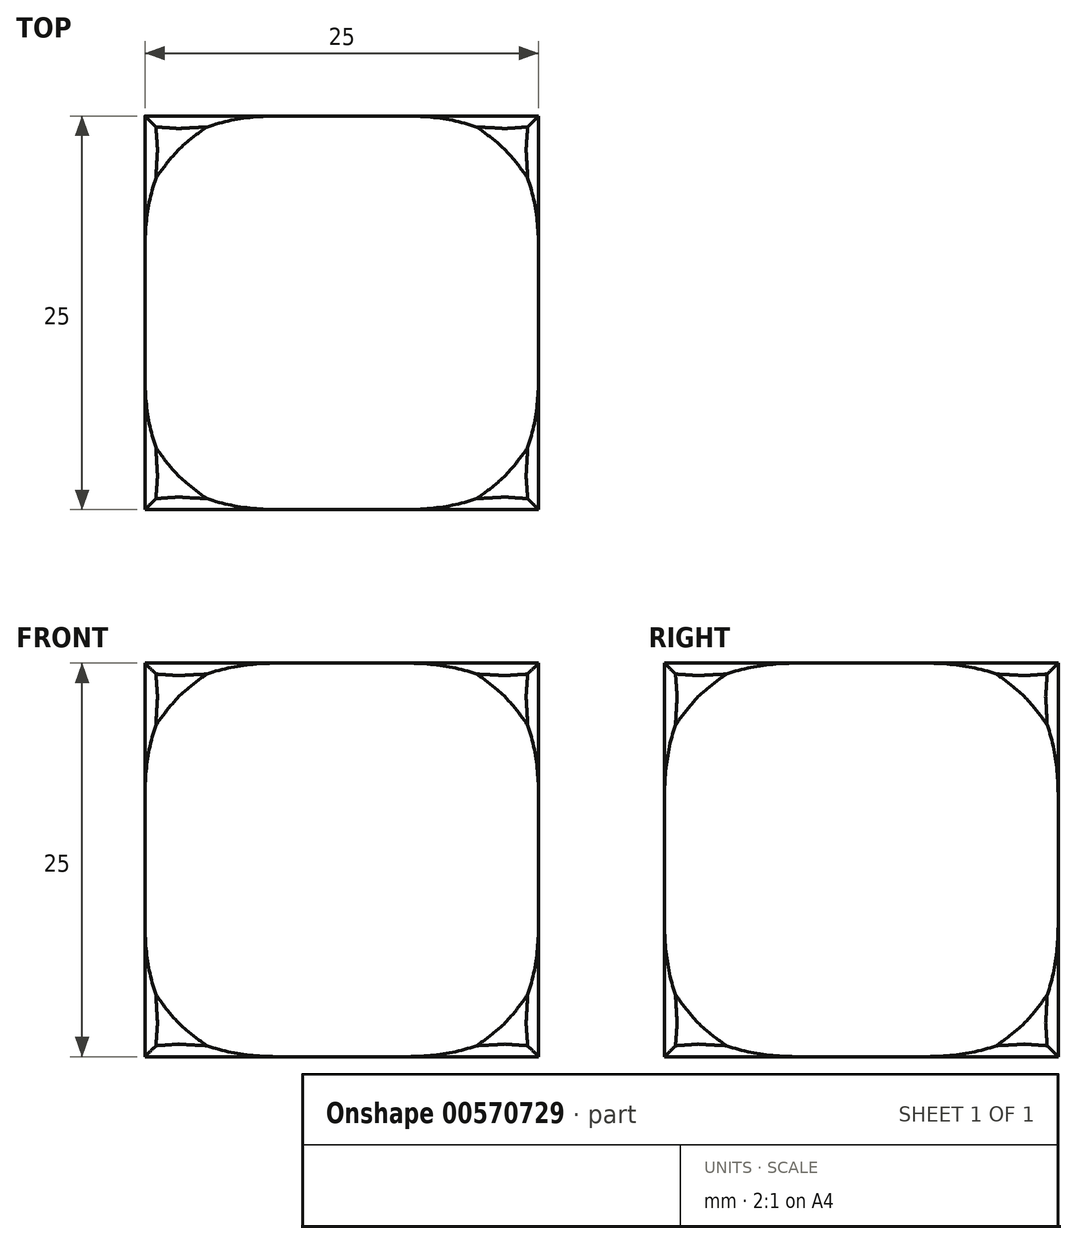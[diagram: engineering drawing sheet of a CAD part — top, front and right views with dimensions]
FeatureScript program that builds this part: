
annotation { "Feature Type Name" : "Feature", "Feature Type Description" : "" }
export const myFeature = defineFeature(function(context is Context, id is Id, definition is map)
    precondition{}
    {
        {
            var Q0;
            Q0=qCreatedBy(makeId("Top.planeOp"),FACE);
            var sketch = newSketch(context, id + "F0", { "sketchPlane" : qUnion([Q0])});
            skLineSegment(sketch, "E0.bottom", {"start": v(-8.3, -12.5) * mm, "end": v(8.3, -12.5) * mm});
            skLineSegment(sketch, "E0.top", {"start": v(-8.3, 12.5) * mm, "end": v(8.3, 12.5) * mm});
            skLineSegment(sketch, "E0.left", {"start": v(-12.5, -8.3) * mm, "end": v(-12.5, 8.3) * mm});
            skLineSegment(sketch, "E0.right", {"start": v(12.5, -8.3) * mm, "end": v(12.5, 8.3) * mm});
            skPoint(sketch, "E0.middle", {"position": v(0, 0) * mm});
            skArc(sketch, "E1", {"start": v(-8.3, 12.5) * mm, "mid": v(-10.6, 10.6) * mm, "end": v(-12.5, 8.3) * mm});
            skPoint(sketch, "E2.orphan", {"position": v(-12.5, 12.5) * mm});
            skPoint(sketch, "E3.orphan", {"position": v(12.5, 12.5) * mm});
            skArc(sketch, "E4.trimOffspring", {"start": v(12.5, 8.3) * mm, "mid": v(10.6, 10.6) * mm, "end": v(8.3, 12.5) * mm});
            skPoint(sketch, "E5.orphan", {"position": v(12.5, -12.5) * mm});
            skArc(sketch, "E6.trimOffspring", {"start": v(8.3, -12.5) * mm, "mid": v(10.6, -10.6) * mm, "end": v(12.5, -8.3) * mm});
            skPoint(sketch, "E7.orphan", {"position": v(-12.5, -12.5) * mm});
            skArc(sketch, "E8.trimOffspring", {"start": v(-12.5, -8.3) * mm, "mid": v(-10.6, -10.6) * mm, "end": v(-8.3, -12.5) * mm});
            skSolve(sketch);
        }
        {
            var Q0;
            Q0=makeQuery(id+"F0.imprint","IMPRINT",FACE,{"disambiguationData":[TD([[makeQuery(id+"F0.imprint","IMPRINT",EDGE,{"derivedFrom":sQuery(id+"F0.wireOp",EDGE,"E0.bottom")}),1.0]])]});
            extrude(context, id + "F1", {"entities" : qUnion([Q0]), "depth" : 25 * mm, "offsetDistance" : 25 * mm});
        }
        {
            var Q0;
            Q0=makeQuery(id+"F1.opExtrude","SWEPT_FACE",FACE,{"disambiguationData":[OSD([sQuery(id+"F0.wireOp",EDGE,"E0.left")])]});
            var sketch = newSketch(context, id + "F2", { "sketchPlane" : qUnion([Q0])});
            skLineSegment(sketch, "E9.bottom", {"start": v(8.3, 0) * mm, "end": v(-8.3, 0) * mm});
            skLineSegment(sketch, "E9.top", {"start": v(8.3, 25) * mm, "end": v(-8.3, 25) * mm});
            skLineSegment(sketch, "E9.left", {"start": v(12.5, 4.2) * mm, "end": v(12.5, 20.8) * mm});
            skLineSegment(sketch, "E9.right", {"start": v(-12.5, 4.2) * mm, "end": v(-12.5, 25) * mm});
            skPoint(sketch, "E9.middle", {"position": v(0, 12.5) * mm});
            skPoint(sketch, "E9.middle.positionSnap0", {"position": v(-8.3, 12.5) * mm});
            skPoint(sketch, "E9.centerSnap0", {"position": v(-8.3, 12.5) * mm});
            skArc(sketch, "E10", {"start": v(-12.5, 4.2) * mm, "mid": v(-10.6, 1.9) * mm, "end": v(-8.3, 0) * mm});
            skPoint(sketch, "E11.orphan", {"position": v(-12.5, 0) * mm});
            skArc(sketch, "E12.trimOffspring", {"start": v(8.3, 0) * mm, "mid": v(10.6, 1.9) * mm, "end": v(12.5, 4.2) * mm});
            skArc(sketch, "E13.trimOffspring", {"start": v(12.5, 20.8) * mm, "mid": v(10.6, 23.1) * mm, "end": v(8.3, 25) * mm});
            skArc(sketch, "E14.trimOffspring", {"start": v(-8.3, 25) * mm, "mid": v(-10.6, 23.1) * mm, "end": v(-12.5, 20.8) * mm});
            skPoint(sketch, "E15.orphan", {"position": v(12.5, 25) * mm});
            skPoint(sketch, "E16.orphan", {"position": v(12.5, 0) * mm});
            skSolve(sketch);
        }
        {
            var Q0;
            Q0=qSketchRegion(id+"F2",true);
            extrude(context, id + "F3", {"entities" : qUnion([Q0]), "operationType" : NewBodyOperationType.ADD, "oppositeDirection" : true, "depth" : 25 * mm, "offsetDistance" : 25 * mm});
        }
        {
            var Q0;
            Q0=makeQuery(id+"F3.boolean.opBoolean","MERGE",FACE,{"derivedFrom":[makeQuery(id+"F1.opExtrude","SWEPT_FACE",FACE,{"disambiguationData":[OSD([sQuery(id+"F0.wireOp",EDGE,"E0.top")])]}),makeQuery(id+"F3.opExtrude","SWEPT_FACE",FACE,{"disambiguationData":[OSD([sQuery(id+"F2.wireOp",EDGE,"E9.right")])]})]});
            var sketch = newSketch(context, id + "F4", { "sketchPlane" : qUnion([Q0])});
            skLineSegment(sketch, "E17.bottom", {"start": v(-8.3, 0) * mm, "end": v(8.3, 0) * mm});
            skLineSegment(sketch, "E17.top", {"start": v(-8.3, 25) * mm, "end": v(8.3, 25) * mm});
            skLineSegment(sketch, "E17.left", {"start": v(-12.5, 4.2) * mm, "end": v(-12.5, 20.8) * mm});
            skLineSegment(sketch, "E17.right", {"start": v(12.5, 4.2) * mm, "end": v(12.5, 20.8) * mm});
            skPoint(sketch, "E17.middle", {"position": v(0, 12.5) * mm});
            skPoint(sketch, "E17.middle.positionSnap0", {"position": v(-12.5, 12.5) * mm});
            skPoint(sketch, "E17.middle.positionSnap1", {"position": v(0, 25) * mm});
            skPoint(sketch, "E17.centerSnap0", {"position": v(-12.5, 12.5) * mm});
            skPoint(sketch, "E17.centerSnap1", {"position": v(0, 25) * mm});
            skArc(sketch, "E18", {"start": v(-8.3, 25) * mm, "mid": v(-10.6, 23.1) * mm, "end": v(-12.5, 20.8) * mm});
            skPoint(sketch, "E19.orphan", {"position": v(-12.5, 25) * mm});
            skArc(sketch, "E20.trimOffspring", {"start": v(-12.5, 4.2) * mm, "mid": v(-10.6, 1.9) * mm, "end": v(-8.3, 0) * mm});
            skPoint(sketch, "E21.orphan", {"position": v(-12.5, 0) * mm});
            skArc(sketch, "E22.trimOffspring", {"start": v(8.3, 0) * mm, "mid": v(10.6, 1.9) * mm, "end": v(12.5, 4.2) * mm});
            skPoint(sketch, "E23.orphan", {"position": v(12.5, 0) * mm});
            skArc(sketch, "E24.trimOffspring", {"start": v(12.5, 20.8) * mm, "mid": v(10.6, 23.1) * mm, "end": v(8.3, 25) * mm});
            skPoint(sketch, "E25.orphan", {"position": v(12.5, 25) * mm});
            skSolve(sketch);
        }
        {
            var Q0;
            Q0=qSketchRegion(id+"F4",true);
            extrude(context, id + "F5", {"entities" : qUnion([Q0]), "operationType" : NewBodyOperationType.ADD, "oppositeDirection" : true, "depth" : 25 * mm, "offsetDistance" : 25 * mm});
        }
        {
            var Q0;
            Q0=makeQuery(id+"F5.opExtrude","CAP_EDGE",EDGE,{"disambiguationData":[OSD([sQuery(id+"F4.wireOp",EDGE,"E18")])],"isStart":false});
            var Q1;
            Q1=makeQuery(id+"F1.opExtrude","CAP_EDGE",EDGE,{"disambiguationData":[OSD([sQuery(id+"F0.wireOp",EDGE,"E6.trimOffspring")])],"isStart":false});
            var Q2;
            Q2=makeQuery(id+"F3.opExtrude","CAP_EDGE",EDGE,{"disambiguationData":[OSD([sQuery(id+"F2.wireOp",EDGE,"E13.trimOffspring")])],"isStart":false});
            var Q3;
            Q3=makeQuery(id+"F5.opExtrude","CAP_EDGE",EDGE,{"disambiguationData":[OSD([sQuery(id+"F4.wireOp",EDGE,"E24.trimOffspring")])],"isStart":false});
            var Q4;
            Q4=makeQuery(id+"F1.opExtrude","CAP_EDGE",EDGE,{"disambiguationData":[OSD([sQuery(id+"F0.wireOp",EDGE,"E8.trimOffspring")])],"isStart":false});
            var Q5;
            Q5=makeQuery(id+"F3.opExtrude","CAP_EDGE",EDGE,{"disambiguationData":[OSD([sQuery(id+"F2.wireOp",EDGE,"E13.trimOffspring")])],"isStart":true});
            var Q6;
            Q6=makeQuery(id+"F5.opExtrude","CAP_EDGE",EDGE,{"disambiguationData":[OSD([sQuery(id+"F4.wireOp",EDGE,"E22.trimOffspring")])],"isStart":false});
            var Q7;
            Q7=makeQuery(id+"F3.opExtrude","CAP_EDGE",EDGE,{"disambiguationData":[OSD([sQuery(id+"F2.wireOp",EDGE,"E12.trimOffspring")])],"isStart":true});
            var Q8;
            Q8=makeQuery(id+"F1.opExtrude","CAP_EDGE",EDGE,{"disambiguationData":[OSD([sQuery(id+"F0.wireOp",EDGE,"E8.trimOffspring")])],"isStart":true});
            var Q9;
            Q9=makeQuery(id+"F5.opExtrude","CAP_EDGE",EDGE,{"disambiguationData":[OSD([sQuery(id+"F4.wireOp",EDGE,"E20.trimOffspring")])],"isStart":false});
            var Q10;
            Q10=makeQuery(id+"F1.opExtrude","CAP_EDGE",EDGE,{"disambiguationData":[OSD([sQuery(id+"F0.wireOp",EDGE,"E6.trimOffspring")])],"isStart":true});
            var Q11;
            Q11=makeQuery(id+"F3.opExtrude","CAP_EDGE",EDGE,{"disambiguationData":[OSD([sQuery(id+"F2.wireOp",EDGE,"E12.trimOffspring")])],"isStart":false});
            var Q12;
            Q12=makeQuery(id+"F3.opExtrude","CAP_EDGE",EDGE,{"disambiguationData":[OSD([sQuery(id+"F2.wireOp",EDGE,"E10")])],"isStart":false});
            var Q13;
            Q13=makeQuery(id+"F5.opExtrude","CAP_EDGE",EDGE,{"disambiguationData":[OSD([sQuery(id+"F4.wireOp",EDGE,"E20.trimOffspring")])],"isStart":true});
            var Q14;
            Q14=makeQuery(id+"F1.opExtrude","CAP_EDGE",EDGE,{"disambiguationData":[OSD([sQuery(id+"F0.wireOp",EDGE,"E4.trimOffspring")])],"isStart":true});
            var Q15;
            Q15=makeQuery(id+"F3.opExtrude","CAP_EDGE",EDGE,{"disambiguationData":[OSD([sQuery(id+"F2.wireOp",EDGE,"E14.trimOffspring")])],"isStart":false});
            var Q16;
            Q16=makeQuery(id+"F5.opExtrude","CAP_EDGE",EDGE,{"disambiguationData":[OSD([sQuery(id+"F4.wireOp",EDGE,"E18")])],"isStart":true});
            var Q17;
            Q17=makeQuery(id+"F1.opExtrude","CAP_EDGE",EDGE,{"disambiguationData":[OSD([sQuery(id+"F0.wireOp",EDGE,"E4.trimOffspring")])],"isStart":false});
            var Q18;
            Q18=makeQuery(id+"F1.opExtrude","CAP_EDGE",EDGE,{"disambiguationData":[OSD([sQuery(id+"F0.wireOp",EDGE,"E1")])],"isStart":false});
            var Q19;
            Q19=makeQuery(id+"F5.opExtrude","CAP_EDGE",EDGE,{"disambiguationData":[OSD([sQuery(id+"F4.wireOp",EDGE,"E24.trimOffspring")])],"isStart":true});
            var Q20;
            Q20=makeQuery(id+"F3.opExtrude","CAP_EDGE",EDGE,{"disambiguationData":[OSD([sQuery(id+"F2.wireOp",EDGE,"E14.trimOffspring")])],"isStart":true});
            var Q21;
            Q21=makeQuery(id+"F3.opExtrude","CAP_EDGE",EDGE,{"disambiguationData":[OSD([sQuery(id+"F2.wireOp",EDGE,"E10")])],"isStart":true});
            var Q22;
            Q22=makeQuery(id+"F5.opExtrude","CAP_EDGE",EDGE,{"disambiguationData":[OSD([sQuery(id+"F4.wireOp",EDGE,"E22.trimOffspring")])],"isStart":true});
            var Q23;
            Q23=makeQuery(id+"F1.opExtrude","CAP_EDGE",EDGE,{"disambiguationData":[OSD([sQuery(id+"F0.wireOp",EDGE,"E1")])],"isStart":true});
            fillet(context, id + "F6", {"entities" : qUnion([Q0, Q1, Q2, Q3, Q4, Q5, Q6, Q7, Q8, Q9, Q10, Q11, Q12, Q13, Q14, Q15, Q16, Q17, Q18, Q19, Q20, Q21, Q22, Q23]), "radius" : 1.88 * mm, "tangentPropagation" : true, "allowEdgeOverflow" : false});
        }
        {
            var Q0;
            Q0=makeQuery(id+"F6.opFillet","BLEND_EDGE",EDGE,{"disambiguationData":[OD(1.0)],"blendedFrom":[makeQuery(id+"F1.opExtrude","CAP_EDGE",EDGE,{"disambiguationData":[OSD([sQuery(id+"F0.wireOp",EDGE,"E6.trimOffspring")])],"isStart":false}),makeQuery(id+"F5.opExtrude","CAP_EDGE",EDGE,{"disambiguationData":[OSD([sQuery(id+"F4.wireOp",EDGE,"E18")])],"isStart":false})],"blendedInto":[]});
            var Q1;
            Q1=makeQuery(id+"F6.opFillet","BLEND_EDGE",EDGE,{"disambiguationData":[OD(1.0)],"blendedFrom":[makeQuery(id+"F1.opExtrude","CAP_EDGE",EDGE,{"disambiguationData":[OSD([sQuery(id+"F0.wireOp",EDGE,"E6.trimOffspring")])],"isStart":false}),makeQuery(id+"F3.opExtrude","CAP_EDGE",EDGE,{"disambiguationData":[OSD([sQuery(id+"F2.wireOp",EDGE,"E13.trimOffspring")])],"isStart":false})],"blendedInto":[]});
            var Q2;
            Q2=makeQuery(id+"F6.opFillet","BLEND_EDGE",EDGE,{"disambiguationData":[OD(1.0)],"blendedFrom":[makeQuery(id+"F3.opExtrude","CAP_EDGE",EDGE,{"disambiguationData":[OSD([sQuery(id+"F2.wireOp",EDGE,"E13.trimOffspring")])],"isStart":false}),makeQuery(id+"F5.opExtrude","CAP_EDGE",EDGE,{"disambiguationData":[OSD([sQuery(id+"F4.wireOp",EDGE,"E18")])],"isStart":false})],"blendedInto":[]});
            var Q3;
            Q3=makeQuery(id+"F6.opFillet","BLEND_EDGE",EDGE,{"disambiguationData":[OD(1.0)],"blendedFrom":[makeQuery(id+"F1.opExtrude","CAP_EDGE",EDGE,{"disambiguationData":[OSD([sQuery(id+"F0.wireOp",EDGE,"E8.trimOffspring")])],"isStart":false}),makeQuery(id+"F5.opExtrude","CAP_EDGE",EDGE,{"disambiguationData":[OSD([sQuery(id+"F4.wireOp",EDGE,"E24.trimOffspring")])],"isStart":false})],"blendedInto":[]});
            var Q4;
            Q4=makeQuery(id+"F6.opFillet","BLEND_EDGE",EDGE,{"disambiguationData":[OD(1.0)],"blendedFrom":[makeQuery(id+"F1.opExtrude","CAP_EDGE",EDGE,{"disambiguationData":[OSD([sQuery(id+"F0.wireOp",EDGE,"E8.trimOffspring")])],"isStart":false}),makeQuery(id+"F3.opExtrude","CAP_EDGE",EDGE,{"disambiguationData":[OSD([sQuery(id+"F2.wireOp",EDGE,"E13.trimOffspring")])],"isStart":true})],"blendedInto":[]});
            var Q5;
            Q5=makeQuery(id+"F6.opFillet","BLEND_EDGE",EDGE,{"disambiguationData":[OD(1.0)],"blendedFrom":[makeQuery(id+"F3.opExtrude","CAP_EDGE",EDGE,{"disambiguationData":[OSD([sQuery(id+"F2.wireOp",EDGE,"E13.trimOffspring")])],"isStart":true}),makeQuery(id+"F5.opExtrude","CAP_EDGE",EDGE,{"disambiguationData":[OSD([sQuery(id+"F4.wireOp",EDGE,"E24.trimOffspring")])],"isStart":false})],"blendedInto":[]});
            var Q6;
            Q6=makeQuery(id+"F6.opFillet","BLEND_EDGE",EDGE,{"disambiguationData":[OD(1.0)],"blendedFrom":[makeQuery(id+"F3.opExtrude","CAP_EDGE",EDGE,{"disambiguationData":[OSD([sQuery(id+"F2.wireOp",EDGE,"E12.trimOffspring")])],"isStart":true}),makeQuery(id+"F5.opExtrude","CAP_EDGE",EDGE,{"disambiguationData":[OSD([sQuery(id+"F4.wireOp",EDGE,"E22.trimOffspring")])],"isStart":false})],"blendedInto":[]});
            var Q7;
            Q7=makeQuery(id+"F6.opFillet","BLEND_EDGE",EDGE,{"disambiguationData":[OD(1.0)],"blendedFrom":[makeQuery(id+"F1.opExtrude","CAP_EDGE",EDGE,{"disambiguationData":[OSD([sQuery(id+"F0.wireOp",EDGE,"E8.trimOffspring")])],"isStart":true}),makeQuery(id+"F5.opExtrude","CAP_EDGE",EDGE,{"disambiguationData":[OSD([sQuery(id+"F4.wireOp",EDGE,"E22.trimOffspring")])],"isStart":false})],"blendedInto":[]});
            var Q8;
            Q8=makeQuery(id+"F6.opFillet","BLEND_EDGE",EDGE,{"disambiguationData":[OD(1.0)],"blendedFrom":[makeQuery(id+"F1.opExtrude","CAP_EDGE",EDGE,{"disambiguationData":[OSD([sQuery(id+"F0.wireOp",EDGE,"E8.trimOffspring")])],"isStart":true}),makeQuery(id+"F3.opExtrude","CAP_EDGE",EDGE,{"disambiguationData":[OSD([sQuery(id+"F2.wireOp",EDGE,"E12.trimOffspring")])],"isStart":true})],"blendedInto":[]});
            var Q9;
            Q9=makeQuery(id+"F6.opFillet","BLEND_EDGE",EDGE,{"disambiguationData":[OD(1.0)],"blendedFrom":[makeQuery(id+"F1.opExtrude","CAP_EDGE",EDGE,{"disambiguationData":[OSD([sQuery(id+"F0.wireOp",EDGE,"E6.trimOffspring")])],"isStart":true}),makeQuery(id+"F5.opExtrude","CAP_EDGE",EDGE,{"disambiguationData":[OSD([sQuery(id+"F4.wireOp",EDGE,"E20.trimOffspring")])],"isStart":false})],"blendedInto":[]});
            var Q10;
            Q10=makeQuery(id+"F6.opFillet","BLEND_EDGE",EDGE,{"disambiguationData":[OD(1.0)],"blendedFrom":[makeQuery(id+"F3.opExtrude","CAP_EDGE",EDGE,{"disambiguationData":[OSD([sQuery(id+"F2.wireOp",EDGE,"E12.trimOffspring")])],"isStart":false}),makeQuery(id+"F5.opExtrude","CAP_EDGE",EDGE,{"disambiguationData":[OSD([sQuery(id+"F4.wireOp",EDGE,"E20.trimOffspring")])],"isStart":false})],"blendedInto":[]});
            var Q11;
            Q11=makeQuery(id+"F6.opFillet","BLEND_EDGE",EDGE,{"disambiguationData":[OD(1.0)],"blendedFrom":[makeQuery(id+"F1.opExtrude","CAP_EDGE",EDGE,{"disambiguationData":[OSD([sQuery(id+"F0.wireOp",EDGE,"E6.trimOffspring")])],"isStart":true}),makeQuery(id+"F3.opExtrude","CAP_EDGE",EDGE,{"disambiguationData":[OSD([sQuery(id+"F2.wireOp",EDGE,"E12.trimOffspring")])],"isStart":false})],"blendedInto":[]});
            var Q12;
            Q12=makeQuery(id+"F6.opFillet","BLEND_EDGE",EDGE,{"disambiguationData":[OD(1.0)],"blendedFrom":[makeQuery(id+"F1.opExtrude","CAP_EDGE",EDGE,{"disambiguationData":[OSD([sQuery(id+"F0.wireOp",EDGE,"E4.trimOffspring")])],"isStart":true}),makeQuery(id+"F5.opExtrude","CAP_EDGE",EDGE,{"disambiguationData":[OSD([sQuery(id+"F4.wireOp",EDGE,"E20.trimOffspring")])],"isStart":true})],"blendedInto":[]});
            var Q13;
            Q13=makeQuery(id+"F6.opFillet","BLEND_EDGE",EDGE,{"disambiguationData":[OD(1.0)],"blendedFrom":[makeQuery(id+"F1.opExtrude","CAP_EDGE",EDGE,{"disambiguationData":[OSD([sQuery(id+"F0.wireOp",EDGE,"E4.trimOffspring")])],"isStart":true}),makeQuery(id+"F3.opExtrude","CAP_EDGE",EDGE,{"disambiguationData":[OSD([sQuery(id+"F2.wireOp",EDGE,"E10")])],"isStart":false})],"blendedInto":[]});
            var Q14;
            Q14=makeQuery(id+"F6.opFillet","BLEND_EDGE",EDGE,{"disambiguationData":[OD(1.0)],"blendedFrom":[makeQuery(id+"F3.opExtrude","CAP_EDGE",EDGE,{"disambiguationData":[OSD([sQuery(id+"F2.wireOp",EDGE,"E10")])],"isStart":false}),makeQuery(id+"F5.opExtrude","CAP_EDGE",EDGE,{"disambiguationData":[OSD([sQuery(id+"F4.wireOp",EDGE,"E20.trimOffspring")])],"isStart":true})],"blendedInto":[]});
            var Q15;
            Q15=makeQuery(id+"F6.opFillet","BLEND_EDGE",EDGE,{"disambiguationData":[OD(1.0)],"blendedFrom":[makeQuery(id+"F1.opExtrude","CAP_EDGE",EDGE,{"disambiguationData":[OSD([sQuery(id+"F0.wireOp",EDGE,"E1")])],"isStart":true}),makeQuery(id+"F5.opExtrude","CAP_EDGE",EDGE,{"disambiguationData":[OSD([sQuery(id+"F4.wireOp",EDGE,"E22.trimOffspring")])],"isStart":true})],"blendedInto":[]});
            var Q16;
            Q16=makeQuery(id+"F6.opFillet","BLEND_EDGE",EDGE,{"disambiguationData":[OD(1.0)],"blendedFrom":[makeQuery(id+"F1.opExtrude","CAP_EDGE",EDGE,{"disambiguationData":[OSD([sQuery(id+"F0.wireOp",EDGE,"E1")])],"isStart":true}),makeQuery(id+"F3.opExtrude","CAP_EDGE",EDGE,{"disambiguationData":[OSD([sQuery(id+"F2.wireOp",EDGE,"E10")])],"isStart":true})],"blendedInto":[]});
            var Q17;
            Q17=makeQuery(id+"F6.opFillet","BLEND_EDGE",EDGE,{"disambiguationData":[OD(1.0)],"blendedFrom":[makeQuery(id+"F3.opExtrude","CAP_EDGE",EDGE,{"disambiguationData":[OSD([sQuery(id+"F2.wireOp",EDGE,"E10")])],"isStart":true}),makeQuery(id+"F5.opExtrude","CAP_EDGE",EDGE,{"disambiguationData":[OSD([sQuery(id+"F4.wireOp",EDGE,"E22.trimOffspring")])],"isStart":true})],"blendedInto":[]});
            var Q18;
            Q18=makeQuery(id+"F6.opFillet","BLEND_EDGE",EDGE,{"disambiguationData":[OD(1.0)],"blendedFrom":[makeQuery(id+"F1.opExtrude","CAP_EDGE",EDGE,{"disambiguationData":[OSD([sQuery(id+"F0.wireOp",EDGE,"E4.trimOffspring")])],"isStart":false}),makeQuery(id+"F5.opExtrude","CAP_EDGE",EDGE,{"disambiguationData":[OSD([sQuery(id+"F4.wireOp",EDGE,"E18")])],"isStart":true})],"blendedInto":[]});
            var Q19;
            Q19=makeQuery(id+"F6.opFillet","BLEND_EDGE",EDGE,{"disambiguationData":[OD(1.0)],"blendedFrom":[makeQuery(id+"F3.opExtrude","CAP_EDGE",EDGE,{"disambiguationData":[OSD([sQuery(id+"F2.wireOp",EDGE,"E14.trimOffspring")])],"isStart":false}),makeQuery(id+"F5.opExtrude","CAP_EDGE",EDGE,{"disambiguationData":[OSD([sQuery(id+"F4.wireOp",EDGE,"E18")])],"isStart":true})],"blendedInto":[]});
            var Q20;
            Q20=makeQuery(id+"F6.opFillet","BLEND_EDGE",EDGE,{"disambiguationData":[OD(1.0)],"blendedFrom":[makeQuery(id+"F1.opExtrude","CAP_EDGE",EDGE,{"disambiguationData":[OSD([sQuery(id+"F0.wireOp",EDGE,"E4.trimOffspring")])],"isStart":false}),makeQuery(id+"F3.opExtrude","CAP_EDGE",EDGE,{"disambiguationData":[OSD([sQuery(id+"F2.wireOp",EDGE,"E14.trimOffspring")])],"isStart":false})],"blendedInto":[]});
            var Q21;
            Q21=makeQuery(id+"F6.opFillet","BLEND_EDGE",EDGE,{"disambiguationData":[OD(1.0)],"blendedFrom":[makeQuery(id+"F1.opExtrude","CAP_EDGE",EDGE,{"disambiguationData":[OSD([sQuery(id+"F0.wireOp",EDGE,"E1")])],"isStart":false}),makeQuery(id+"F5.opExtrude","CAP_EDGE",EDGE,{"disambiguationData":[OSD([sQuery(id+"F4.wireOp",EDGE,"E24.trimOffspring")])],"isStart":true})],"blendedInto":[]});
            var Q22;
            Q22=makeQuery(id+"F6.opFillet","BLEND_EDGE",EDGE,{"disambiguationData":[OD(1.0)],"blendedFrom":[makeQuery(id+"F3.opExtrude","CAP_EDGE",EDGE,{"disambiguationData":[OSD([sQuery(id+"F2.wireOp",EDGE,"E14.trimOffspring")])],"isStart":true}),makeQuery(id+"F5.opExtrude","CAP_EDGE",EDGE,{"disambiguationData":[OSD([sQuery(id+"F4.wireOp",EDGE,"E24.trimOffspring")])],"isStart":true})],"blendedInto":[]});
            var Q23;
            Q23=makeQuery(id+"F6.opFillet","BLEND_EDGE",EDGE,{"disambiguationData":[OD(1.0)],"blendedFrom":[makeQuery(id+"F1.opExtrude","CAP_EDGE",EDGE,{"disambiguationData":[OSD([sQuery(id+"F0.wireOp",EDGE,"E1")])],"isStart":false}),makeQuery(id+"F3.opExtrude","CAP_EDGE",EDGE,{"disambiguationData":[OSD([sQuery(id+"F2.wireOp",EDGE,"E14.trimOffspring")])],"isStart":true})],"blendedInto":[]});
            chamfer(context, id + "F7", {"entities" : qUnion([Q0, Q1, Q2, Q3, Q4, Q5, Q6, Q7, Q8, Q9, Q10, Q11, Q12, Q13, Q14, Q15, Q16, Q17, Q18, Q19, Q20, Q21, Q22, Q23]), "width" : 500 * mm, "tangentPropagation" : true});
        }
    });
